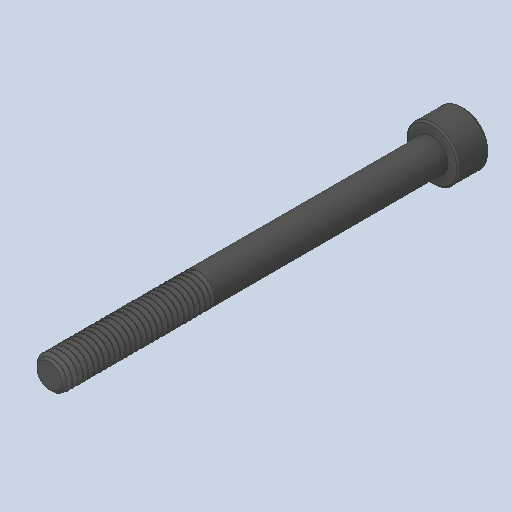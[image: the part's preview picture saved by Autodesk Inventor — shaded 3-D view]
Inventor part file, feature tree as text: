
AUTODESK INVENTOR PART (.ipt)
format: ipt  version: 2023.4 (Build 274418000, 418)  size: 668,160 bytes
history: native  units: in
note: dims shown in document units (in); Inventor stores cm internally (conversion verified against a paired STEP export)
features: chamfer x1
ambient origin geometry x8: Origin, YZ Plane, XZ Plane, XY Plane, X Axis, Y Axis, Z Axis, Center Point
bodies: Solid1 (feature_tree)
feature tree (1):
  chamfer  "Chamfer2"  [1 undecoded]
note: 1 required parameter value undecoded (feature->parameter linkage not recoverable at this tier; creation-order binding heuristic only, values carry confidence <= 0.55)
